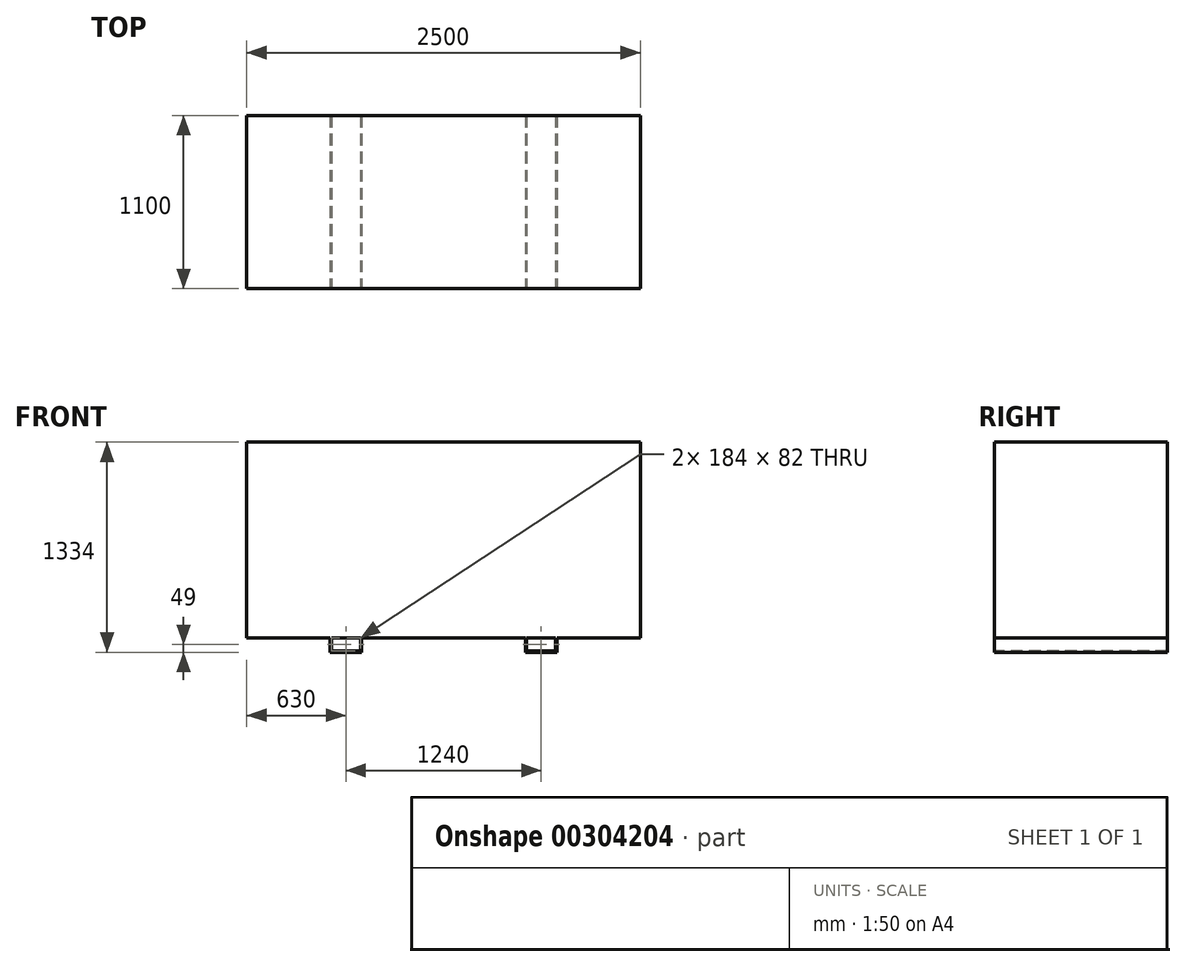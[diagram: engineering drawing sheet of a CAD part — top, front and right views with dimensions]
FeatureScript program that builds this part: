
annotation { "Feature Type Name" : "Feature", "Feature Type Description" : "" }
export const myFeature = defineFeature(function(context is Context, id is Id, definition is map)
    precondition{}
    {
        {
            var Q0;
            Q0=qCreatedBy(makeId("Top.planeOp"),FACE);
            var sketch = newSketch(context, id + "F0", { "sketchPlane" : qUnion([Q0])});
            skLineSegment(sketch, "E0.bottom", {"start": v(0, 0) * mm, "end": v(2500, 0) * mm});
            skLineSegment(sketch, "E0.top", {"start": v(0, -1100) * mm, "end": v(2500, -1100) * mm});
            skLineSegment(sketch, "E0.left", {"start": v(0, 0) * mm, "end": v(0, -1100) * mm});
            skLineSegment(sketch, "E0.right", {"start": v(2500, 0) * mm, "end": v(2500, -1100) * mm});
            skSolve(sketch);
        }
        {
            var Q0;
            Q0=qSketchRegion(id+"F0",true);
            extrude(context, id + "F1", {"entities" : qUnion([Q0]), "depth" : 1334 * mm});
        }
        {
            var Q0;
            Q0=makeQuery(id+"F1.opExtrude","SWEPT_FACE",FACE,{"disambiguationData":[OSD([sQuery(id+"F0.wireOp",EDGE,"E0.top")])]});
            var sketch = newSketch(context, id + "F2", { "sketchPlane" : qUnion([Q0])});
            skLineSegment(sketch, "E1.bottom", {"start": v(0, 0) * mm, "end": v(530, 0) * mm});
            skLineSegment(sketch, "E1.top", {"start": v(0, 90) * mm, "end": v(530, 90) * mm});
            skLineSegment(sketch, "E1.left", {"start": v(0, 0) * mm, "end": v(0, 90) * mm});
            skLineSegment(sketch, "E1.right", {"start": v(530, 0) * mm, "end": v(530, 90) * mm});
            skLineSegment(sketch, "E2.bottom", {"start": v(730, 0) * mm, "end": v(1770, 0) * mm});
            skLineSegment(sketch, "E2.top", {"start": v(730, 90) * mm, "end": v(1770, 90) * mm});
            skLineSegment(sketch, "E2.left", {"start": v(730, 0) * mm, "end": v(730, 90) * mm});
            skLineSegment(sketch, "E2.right", {"start": v(1770, 0) * mm, "end": v(1770, 90) * mm});
            skLineSegment(sketch, "E3.bottom", {"start": v(1970, 90) * mm, "end": v(2500, 90) * mm});
            skLineSegment(sketch, "E3.top", {"start": v(1970, 0) * mm, "end": v(2500, 0) * mm});
            skLineSegment(sketch, "E3.left", {"start": v(1970, 90) * mm, "end": v(1970, 0) * mm});
            skLineSegment(sketch, "E3.right", {"start": v(2500, 90) * mm, "end": v(2500, 0) * mm});
            skLineSegment(sketch, "E4.bottom", {"start": v(538, 90) * mm, "end": v(722, 90) * mm});
            skLineSegment(sketch, "E4.top", {"start": v(538, 8) * mm, "end": v(722, 8) * mm});
            skLineSegment(sketch, "E4.left", {"start": v(538, 90) * mm, "end": v(538, 8) * mm});
            skLineSegment(sketch, "E4.right", {"start": v(722, 90) * mm, "end": v(722, 8) * mm});
            skLineSegment(sketch, "E5.bottom", {"start": v(1778, 90) * mm, "end": v(1962, 90) * mm});
            skLineSegment(sketch, "E5.top", {"start": v(1778, 8) * mm, "end": v(1962, 8) * mm});
            skLineSegment(sketch, "E5.left", {"start": v(1778, 90) * mm, "end": v(1778, 8) * mm});
            skLineSegment(sketch, "E5.right", {"start": v(1962, 90) * mm, "end": v(1962, 8) * mm});
            skSolve(sketch);
        }
        {
            var Q0;
            Q0=qSketchRegion(id+"F2",true);
            extrude(context, id + "F3", {"entities" : qUnion([Q0]), "operationType" : NewBodyOperationType.REMOVE, "endBound" : BoundingType.THROUGH_ALL, "oppositeDirection" : true, "depth" : 25 * mm});
        }
    });
